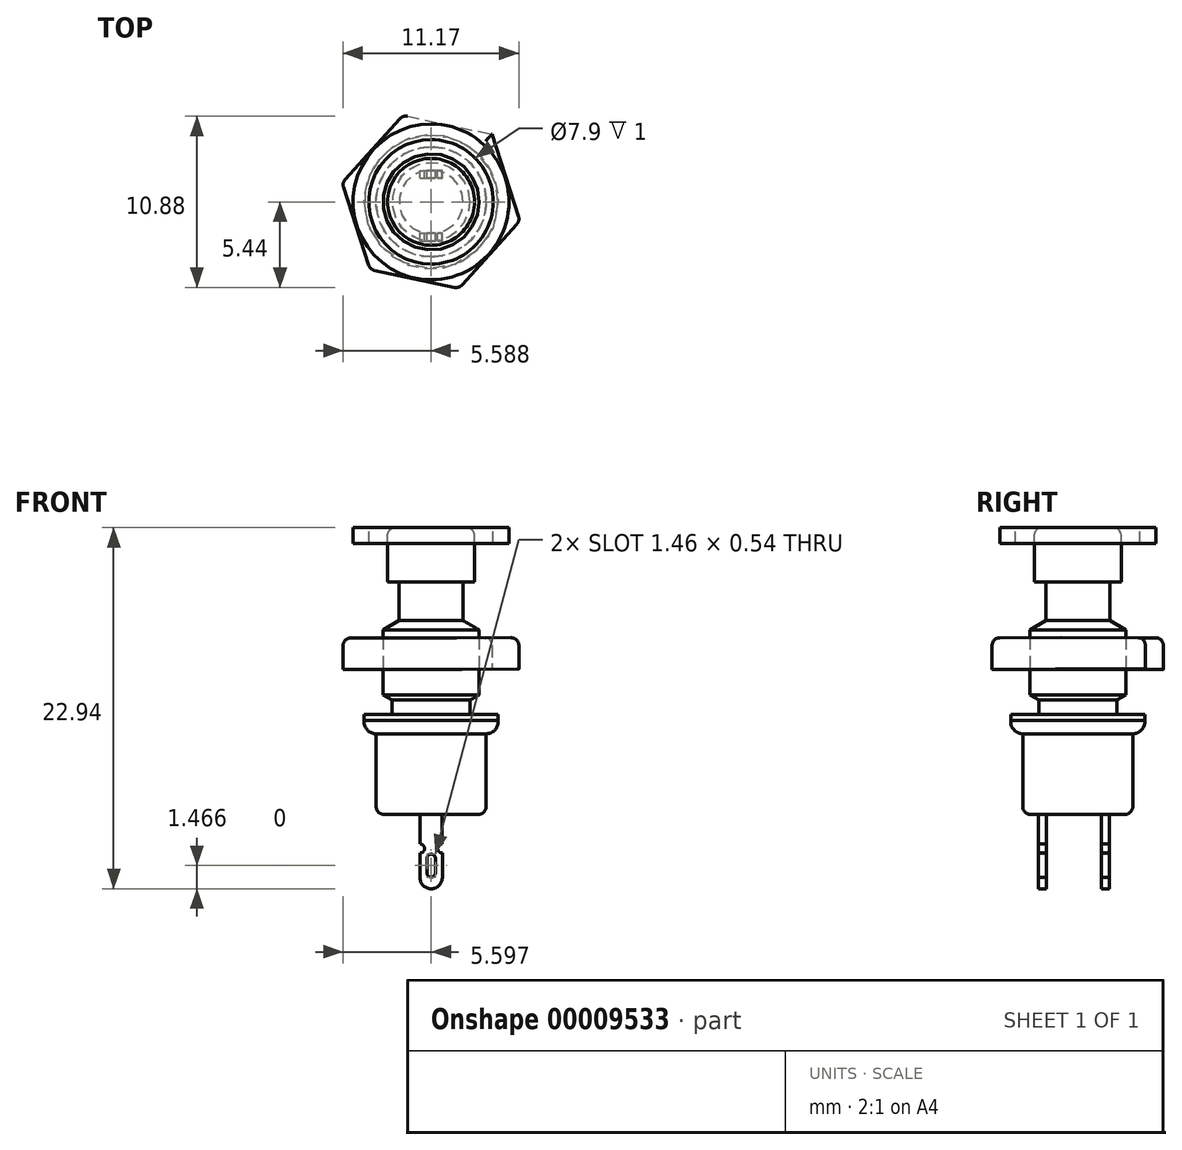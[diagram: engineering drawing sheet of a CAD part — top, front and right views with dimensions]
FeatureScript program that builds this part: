
annotation { "Feature Type Name" : "Feature", "Feature Type Description" : "" }
export const myFeature = defineFeature(function(context is Context, id is Id, definition is map)
    precondition{}
    {
        {
            var Q0;
            Q0=qCreatedBy(makeId("Front.planeOp"),FACE);
            var sketch = newSketch(context, id + "F0", { "sketchPlane" : qUnion([Q0])});
            skLineSegment(sketch, "E0", {"start": v(-3.15, 14.3) * mm, "end": v(-5.91, 14.3) * mm});
            skLineSegment(sketch, "E1", {"start": v(-3.15, 10.84) * mm, "end": v(-5.91, 10.84) * mm});
            skLineSegment(sketch, "E2", {"start": v(-5.18, 10.84) * mm, "end": v(-5.18, 8.4) * mm});
            skLineSegment(sketch, "E3", {"start": v(-5.18, 8.4) * mm, "end": v(-6.2, 7.8) * mm});
            skLineSegment(sketch, "E4", {"start": v(-6.2, 7.8) * mm, "end": v(-6.2, 3.67) * mm});
            skLineSegment(sketch, "E5", {"start": v(-6.2, 3.67) * mm, "end": v(-5.63, 3.34) * mm});
            skLineSegment(sketch, "E6", {"start": v(-5.63, 3.34) * mm, "end": v(-5.63, 2.42) * mm});
            skLineSegment(sketch, "E7", {"start": v(-5.63, 2.42) * mm, "end": v(-7.4, 2.42) * mm});
            skArc(sketch, "E8", {"start": v(-7.4, 2.05) * mm, "mid": v(-7.2, 1.45) * mm, "end": v(-6.64, 1.2) * mm});
            skLineSegment(sketch, "E9", {"start": v(-3.85, -3.92) * mm, "end": v(-3.85, -5.8) * mm});
            skLineSegment(sketch, "E10", {"start": v(-3.85, -6.38) * mm, "end": v(-3.85, -7.9) * mm});
            skArc(sketch, "E11", {"start": v(-3.41, -7.63) * mm, "mid": v(-3.14, -7.9) * mm, "end": v(-2.87, -7.63) * mm});
            skLineSegment(sketch, "E12", {"start": v(-2.87, -7.63) * mm, "end": v(-2.87, -6.71) * mm});
            skArc(sketch, "E13", {"start": v(-2.87, -6.71) * mm, "mid": v(-3.14, -6.44) * mm, "end": v(-3.42, -6.72) * mm});
            skLineSegment(sketch, "E14", {"start": v(-3.42, -6.72) * mm, "end": v(-3.41, -7.63) * mm});
            skLineSegment(sketch, "E15", {"start": v(-3.15, 19) * mm, "end": v(-3.14, -19) * mm, "construction": true});
            skLineSegment(sketch, "E16", {"start": v(-7.4, 2.05) * mm, "end": v(-7.4, 2.42) * mm});
            skLineSegment(sketch, "E17.MirrorCS", {"start": v(-2.44, -6.37) * mm, "end": v(-2.44, -7.9) * mm});
            skLineSegment(sketch, "E18.MirrorCS", {"start": v(-2.44, -3.92) * mm, "end": v(-2.44, -5.8) * mm});
            skLineSegment(sketch, "E19", {"start": v(-3.14, -3.92) * mm, "end": v(-2.44, -3.92) * mm});
            skArc(sketch, "E20", {"start": v(-3.85, -7.9) * mm, "mid": v(-3.14, -8.64) * mm, "end": v(-2.44, -7.9) * mm});
            skLineSegment(sketch, "E21", {"start": v(-3.85, -7.9) * mm, "end": v(-3.85, -7.9) * mm});
            skLineSegment(sketch, "E22.trimOffspring", {"start": v(-2.44, -7.9) * mm, "end": v(-2.44, -7.9) * mm});
            skLineSegment(sketch, "E23", {"start": v(-6.64, 1.2) * mm, "end": v(-3.15, 1.2) * mm});
            skPoint(sketch, "E24.end.orphan", {"position": v(-3.85, -5.8) * mm});
            skPoint(sketch, "E24.start.orphan", {"position": v(-3.85, -6.38) * mm});
            skPoint(sketch, "E25.MirrorCS.end.orphan", {"position": v(-2.44, -5.8) * mm});
            skPoint(sketch, "E25.MirrorCS.start.orphan", {"position": v(-2.44, -6.37) * mm});
            skArc(sketch, "E26", {"start": v(-3.85, -6.38) * mm, "mid": v(-3.56, -6.09) * mm, "end": v(-3.85, -5.8) * mm});
            skArc(sketch, "E27", {"start": v(-2.44, -5.8) * mm, "mid": v(-2.72, -6.09) * mm, "end": v(-2.44, -6.37) * mm});
            skLineSegment(sketch, "E28", {"start": v(-5.91, 10.84) * mm, "end": v(-5.91, 14.3) * mm});
            skLineSegment(sketch, "E29", {"start": v(-3.15, 14.3) * mm, "end": v(-3.14, -3.92) * mm});
            skLineSegment(sketch, "E30", {"start": v(-3.85, -3.92) * mm, "end": v(-3.14, -3.92) * mm});
            skLineSegment(sketch, "E31", {"start": v(-3.14, -3.92) * mm, "end": v(-3.85, -3.92) * mm});
            skLineSegment(sketch, "E32", {"start": v(-6.64, 1.2) * mm, "end": v(-6.64, -3.92) * mm});
            skLineSegment(sketch, "E33", {"start": v(-6.64, -3.92) * mm, "end": v(-3.14, -3.92) * mm});
            skSolve(sketch);
        }
        {
            var Q0;
            {var subQ4=sQuery(id+"F0.wireOp",EDGE,"E0");Q0=makeQuery(id+"F0.imprint","IMPRINT",FACE,{"disambiguationData":[TD([[makeQuery(id+"F0.imprint","IMPRINT",EDGE,{"derivedFrom":subQ4}),1.0]])]});}
            var Q1;
            Q1=sQuery(id+"F0.wireOp",EDGE,"E15");
            revolve(context, id + "F1", {"entities" : qUnion([Q0]), "axis" : qUnion([Q1]), "revolveType" : RevolveType.FULL});
        }
        {
            var Q0;
            {var subQ4=sQuery(id+"F0.wireOp",EDGE,"E2");Q0=makeQuery(id+"F0.imprint","IMPRINT",FACE,{"disambiguationData":[TD([[makeQuery(id+"F0.imprint","IMPRINT",EDGE,{"derivedFrom":subQ4}),1.0]])]});}
            var Q1;
            Q1=sQuery(id+"F0.wireOp",EDGE,"E15");
            revolve(context, id + "F2", {"entities" : qUnion([Q0]), "axis" : qUnion([Q1]), "revolveType" : RevolveType.FULL});
        }
        {
            var Q0;
            {var subQ0=sQuery(id+"F0.wireOp",EDGE,"E32");Q0=makeQuery(id+"F0.imprint","IMPRINT",FACE,{"disambiguationData":[TD([[makeQuery(id+"F0.imprint","IMPRINT",EDGE,{"derivedFrom":subQ0}),1.0]])]});}
            var Q1;
            Q1=sQuery(id+"F0.wireOp",EDGE,"E15");
            revolve(context, id + "F3", {"entities" : qUnion([Q0]), "axis" : qUnion([Q1]), "revolveType" : RevolveType.FULL});
        }
        {
            var Q0;
            Q0=makeQuery(id+"F0.imprint","IMPRINT",FACE,{"disambiguationData":[TD([[makeQuery(id+"F0.imprint","IMPRINT",EDGE,{"derivedFrom":sQuery(id+"F0.wireOp",EDGE,"E9")}),1.0]])]});
            extrude(context, id + "F4", {"entities" : qUnion([Q0]), "depth" : .5 * mm});
        }
        {
            var Q0;
            Q0=makeQuery(id+"F4.opExtrude","SWEPT_BODY",BODY,{"disambiguationData":[OSD([sQuery(id+"F0.wireOp",EDGE,"E9"),sQuery(id+"F0.wireOp",EDGE,"E10"),sQuery(id+"F0.wireOp",EDGE,"E11"),sQuery(id+"F0.wireOp",EDGE,"E12"),sQuery(id+"F0.wireOp",EDGE,"E13"),sQuery(id+"F0.wireOp",EDGE,"E14"),sQuery(id+"F0.wireOp",EDGE,"E17.MirrorCS"),sQuery(id+"F0.wireOp",EDGE,"E18.MirrorCS"),sQuery(id+"F0.wireOp",EDGE,"E19"),sQuery(id+"F0.wireOp",EDGE,"E20"),sQuery(id+"F0.wireOp",EDGE,"E21"),sQuery(id+"F0.wireOp",EDGE,"E22.trimOffspring"),sQuery(id+"F0.wireOp",EDGE,"E26"),sQuery(id+"F0.wireOp",EDGE,"E27"),sQuery(id+"F0.wireOp",EDGE,"E31")])]});
            transform(context, id + "F5", {"entities" : qUnion([Q0]), "transformType" : TransformType.TRANSLATION_3D, "dx" : 0 * mm, "dy" : 2 * mm, "dz" : 0 * mm, "makeCopy" : false});
        }
        {
            var Q0;
            Q0=makeQuery(id+"F4.opExtrude","SWEPT_BODY",BODY,{"disambiguationData":[OSD([sQuery(id+"F0.wireOp",EDGE,"E9"),sQuery(id+"F0.wireOp",EDGE,"E10"),sQuery(id+"F0.wireOp",EDGE,"E11"),sQuery(id+"F0.wireOp",EDGE,"E12"),sQuery(id+"F0.wireOp",EDGE,"E13"),sQuery(id+"F0.wireOp",EDGE,"E14"),sQuery(id+"F0.wireOp",EDGE,"E17.MirrorCS"),sQuery(id+"F0.wireOp",EDGE,"E18.MirrorCS"),sQuery(id+"F0.wireOp",EDGE,"E19"),sQuery(id+"F0.wireOp",EDGE,"E20"),sQuery(id+"F0.wireOp",EDGE,"E21"),sQuery(id+"F0.wireOp",EDGE,"E22.trimOffspring"),sQuery(id+"F0.wireOp",EDGE,"E26"),sQuery(id+"F0.wireOp",EDGE,"E27"),sQuery(id+"F0.wireOp",EDGE,"E31")])]});
            transform(context, id + "F6", {"entities" : qUnion([Q0]), "transformType" : TransformType.TRANSLATION_3D, "dx" : 0 * mm, "dy" : -4 * mm, "dz" : 0 * mm, "makeCopy" : true});
        }
        {
            var Q0;
            Q0=makeQuery(id+"F1.opRevolve","SWEPT_FACE",FACE,{"disambiguationData":[OSD([sQuery(id+"F0.wireOp",EDGE,"E0")])]});
            var sketch = newSketch(context, id + "F7", { "sketchPlane" : qUnion([Q0])});
            skCircle(sketch, "E34.cCircle", {"center": v(-3.15, 0) * mm, "radius": 5 * mm, "construction": true});
            skLineSegment(sketch, "E34.0", {"start": v(-4.93, 5.49) * mm, "end": v(0.71, 4.3) * mm});
            skLineSegment(sketch, "E34.1", {"start": v(0.71, 4.3) * mm, "end": v(2.5, -1.2) * mm});
            skLineSegment(sketch, "E34.2", {"start": v(2.5, -1.2) * mm, "end": v(-1.36, -5.49) * mm});
            skLineSegment(sketch, "E34.3", {"start": v(-1.36, -5.49) * mm, "end": v(-7, -4.3) * mm});
            skLineSegment(sketch, "E34.4", {"start": v(-7, -4.3) * mm, "end": v(-8.8, 1.2) * mm});
            skLineSegment(sketch, "E34.5", {"start": v(-8.8, 1.2) * mm, "end": v(-4.93, 5.49) * mm});
            skPoint(sketch, "E34.0.midPoint", {"position": v(-2.1, 4.9) * mm});
            skCircle(sketch, "E35", {"center": v(-3.15, 0) * mm, "radius": 4.95 * mm});
            skCircle(sketch, "E36.0", {"center": v(-3.15, 0) * mm, "radius": 3.95 * mm});
            skSolve(sketch);
        }
        {
            var Q0;
            Q0=makeQuery(id+"F7.imprint","IMPRINT",FACE,{"disambiguationData":[TD([[makeQuery(id+"F7.imprint","IMPRINT",EDGE,{"derivedFrom":sQuery(id+"F7.wireOp",EDGE,"E34.0")}),-1.0]])]});
            var Q1;
            Q1=makeQuery(id+"F7.imprint","IMPRINT",FACE,{"disambiguationData":[TD([[makeQuery(id+"F7.imprint","IMPRINT",EDGE,{"derivedFrom":sQuery(id+"F7.wireOp",EDGE,"E35")}),1.0]])]});
            var Q2;
            Q2=makeQuery(id+"F7.imprint","IMPRINT",FACE,{"disambiguationData":[TD([[makeQuery(id+"F7.imprint","IMPRINT",EDGE,{"derivedFrom":sQuery(id+"F7.wireOp",EDGE,"E36.0")}),1.0]])]});
            extrude(context, id + "F8", {"entities" : qUnion([Q0, Q1, Q2]), "depth" : 2 * mm});
        }
        {
            var Q0;
            Q0=makeQuery(id+"F1.opRevolve","SWEPT_EDGE",EDGE,{"disambiguationData":[OSD([sQuery(id+"F0.wireOp",EDGE,"E0"),sQuery(id+"F0.wireOp",EDGE,"E28")])]});
            var Q1;
            Q1=makeQuery(id+"F3.opRevolve","SWEPT_EDGE",EDGE,{"disambiguationData":[OSD([sQuery(id+"F0.wireOp",EDGE,"E32"),sQuery(id+"F0.wireOp",EDGE,"E33")])]});
            var Q2;
            Q2=makeQuery(id+"F8.opExtrude","CAP_EDGE",EDGE,{"disambiguationData":[OSD([sQuery(id+"F7.wireOp",EDGE,"E34.2")])],"isStart":false});
            var Q3;
            Q3=makeQuery(id+"F8.opExtrude","CAP_EDGE",EDGE,{"disambiguationData":[OSD([sQuery(id+"F7.wireOp",EDGE,"E34.1")])],"isStart":false});
            var Q4;
            Q4=makeQuery(id+"F8.opExtrude","CAP_EDGE",EDGE,{"disambiguationData":[OSD([sQuery(id+"F7.wireOp",EDGE,"E34.5")])],"isStart":false});
            var Q5;
            Q5=makeQuery(id+"F8.opExtrude","CAP_EDGE",EDGE,{"disambiguationData":[OSD([sQuery(id+"F7.wireOp",EDGE,"E34.4")])],"isStart":false});
            var Q6;
            Q6=makeQuery(id+"F8.opExtrude","CAP_EDGE",EDGE,{"disambiguationData":[OSD([sQuery(id+"F7.wireOp",EDGE,"E34.3")])],"isStart":false});
            var Q7;
            Q7=makeQuery(id+"F8.opExtrude","CAP_EDGE",EDGE,{"disambiguationData":[OSD([sQuery(id+"F7.wireOp",EDGE,"E34.0")])],"isStart":false});
            var Q8;
            Q8=makeQuery(id+"F8.opExtrude","SWEPT_EDGE",EDGE,{"disambiguationData":[OSD([sQuery(id+"F7.wireOp",EDGE,"E34.0"),sQuery(id+"F7.wireOp",EDGE,"E34.5")])]});
            var Q9;
            Q9=makeQuery(id+"F8.opExtrude","SWEPT_EDGE",EDGE,{"disambiguationData":[OSD([sQuery(id+"F7.wireOp",EDGE,"E34.4"),sQuery(id+"F7.wireOp",EDGE,"E34.5")])]});
            var Q10;
            Q10=makeQuery(id+"F8.opExtrude","SWEPT_EDGE",EDGE,{"disambiguationData":[OSD([sQuery(id+"F7.wireOp",EDGE,"E34.3"),sQuery(id+"F7.wireOp",EDGE,"E34.4")])]});
            var Q11;
            Q11=makeQuery(id+"F8.opExtrude","SWEPT_EDGE",EDGE,{"disambiguationData":[OSD([sQuery(id+"F7.wireOp",EDGE,"E34.2"),sQuery(id+"F7.wireOp",EDGE,"E34.3")])]});
            var Q12;
            Q12=makeQuery(id+"F8.opExtrude","SWEPT_EDGE",EDGE,{"disambiguationData":[OSD([sQuery(id+"F7.wireOp",EDGE,"E34.1"),sQuery(id+"F7.wireOp",EDGE,"E34.2")])]});
            fillet(context, id + "F9", {"entities" : qUnion([Q0, Q1, Q2, Q3, Q4, Q5, Q6, Q7, Q8, Q9, Q10, Q11, Q12]), "radius" : .5 * mm, "tangentPropagation" : true, "allowEdgeOverflow" : false});
        }
        {
            var Q0;
            Q0=makeQuery(id+"F8.opExtrude","SWEPT_BODY",BODY,{"disambiguationData":[OSD([sQuery(id+"F0.wireOp",EDGE,"E0"),sQuery(id+"F0.wireOp",EDGE,"E28"),sQuery(id+"F7.wireOp",EDGE,"E34.0"),sQuery(id+"F7.wireOp",EDGE,"E34.1"),sQuery(id+"F7.wireOp",EDGE,"E34.2"),sQuery(id+"F7.wireOp",EDGE,"E34.3"),sQuery(id+"F7.wireOp",EDGE,"E34.4"),sQuery(id+"F7.wireOp",EDGE,"E34.5")])]});
            transform(context, id + "F10", {"entities" : qUnion([Q0]), "transformType" : TransformType.TRANSLATION_3D, "dx" : 0 * mm, "dy" : 0 * mm, "dz" : -9 * mm, "makeCopy" : false});
        }
        {
            var Q0;
            Q0=makeQuery(id+"F2.opRevolve","SWEPT_BODY",BODY,{"disambiguationData":[OSD([sQuery(id+"F0.wireOp",EDGE,"E1"),sQuery(id+"F0.wireOp",EDGE,"E2"),sQuery(id+"F0.wireOp",EDGE,"E3"),sQuery(id+"F0.wireOp",EDGE,"E4"),sQuery(id+"F0.wireOp",EDGE,"E5"),sQuery(id+"F0.wireOp",EDGE,"E6"),sQuery(id+"F0.wireOp",EDGE,"E7"),sQuery(id+"F0.wireOp",EDGE,"E8"),sQuery(id+"F0.wireOp",EDGE,"E16"),sQuery(id+"F0.wireOp",EDGE,"E23"),sQuery(id+"F0.wireOp",EDGE,"E29")])]});
            var Q1;
            Q1=makeQuery(id+"F8.opExtrude","SWEPT_BODY",BODY,{"disambiguationData":[OSD([sQuery(id+"F0.wireOp",EDGE,"E0"),sQuery(id+"F0.wireOp",EDGE,"E28"),sQuery(id+"F7.wireOp",EDGE,"E34.0"),sQuery(id+"F7.wireOp",EDGE,"E34.1"),sQuery(id+"F7.wireOp",EDGE,"E34.2"),sQuery(id+"F7.wireOp",EDGE,"E34.3"),sQuery(id+"F7.wireOp",EDGE,"E34.4"),sQuery(id+"F7.wireOp",EDGE,"E34.5")])]});
            booleanBodies(context, id + "F11", {"operationType" : BooleanOperationType.SUBTRACTION, "tools" : qUnion([Q0]), "targets" : qUnion([Q1]), "keepTools" : true});
        }
        {
            var Q0;
            Q0=makeQuery(id+"F7.imprint","IMPRINT",FACE,{"disambiguationData":[TD([[makeQuery(id+"F7.imprint","IMPRINT",EDGE,{"derivedFrom":sQuery(id+"F7.wireOp",EDGE,"E35")}),1.0]])]});
            extrude(context, id + "F12", {"entities" : qUnion([Q0]), "oppositeDirection" : true, "depth" : 1 * mm});
        }
    });
